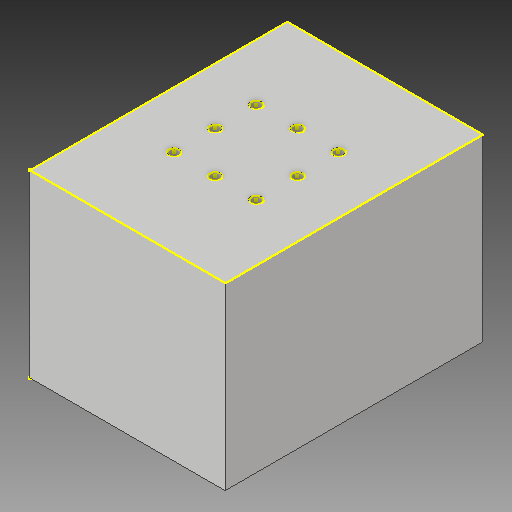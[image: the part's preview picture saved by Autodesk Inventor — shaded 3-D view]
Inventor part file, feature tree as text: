
AUTODESK INVENTOR PART (.ipt)
format: ipt  version: 2017 (Build 210142000, 142)  size: 121,856 bytes
history: native  units: mm
features: sketch x4, extrude x2, projected_geometry x1
ambient origin geometry x8: Origin, YZ Plane, XZ Plane, XY Plane, X Axis, Y Axis, Z Axis, Center Point
bodies: Solide1 (feature_tree)
feature tree (7):
  extrude  "Extrusion1"  Depth=35.0mm
  sketch  "Esquisse2"
  extrude  "Extrusion2"  Depth=50.0mm
  sketch  "Esquisse4"
  sketch  "Esquisse1"
  sketch  "Esquisse3"
  projected_geometry  "Boucle projetée1"
